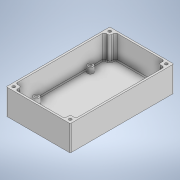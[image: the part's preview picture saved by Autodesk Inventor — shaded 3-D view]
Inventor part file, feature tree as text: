
AUTODESK INVENTOR PART (.ipt)
format: ipt  version: 2021 (Build 250183000, 183)  size: 371,200 bytes
history: native  units: mm
features: fillet x7, extrude x6, sketch x6
ambient origin geometry x8: Origin, YZ Plane, XZ Plane, XY Plane, X Axis, Y Axis, Z Axis, Center Point
bodies: Solid1 (feature_tree)
feature tree (19):
  extrude  "Extrusion1"  Depth=62.0mm
  extrude  "Extrusion2"  Depth=3.0mm
  extrude  "Extrusion3"  Depth=3.0mm
  extrude  "Extrusion4"  Depth=3.0mm
  fillet  "Fillet1"  Radius=6.0mm
  fillet  "Fillet2"  Radius=3.0mm
  fillet  "Fillet3"  Radius=57.4mm
  extrude  "Extrusion5"  Depth=0.8mm
  fillet  "Fillet4"  Radius=51.56mm
  extrude  "Extrusion6"  Depth=6.0mm
  fillet  "Fillet5"  Radius=6.0mm
  fillet  "Fillet6"  Radius=6.0mm
  fillet  "Fillet7"  Radius=20.0mm
  sketch  "Sketch2"  dims[d14=66.0mm d15=62.0mm]
  sketch  "Sketch4"  dims[d16=3.0mm d17=3.0mm]
  sketch  "Sketch5"  dims[d18=3.0mm d19=3.0mm]
  sketch  "Sketch6"  dims[d20=3.0mm d21=4.5mm d22=6.0mm d23=3.0mm d24=57.4mm]
  sketch  "Sketch8"  dims[d25=54.35mm d26=0.8mm d27=51.56mm]
  sketch  "Sketch9"  dims[d28=4.8mm d29=6.0mm d30=6.0mm d31=6.0mm d32=20.0mm d33=20.0mm d34=1.0mm d35=1.0mm d36=2.0mm d37=0.0mm d38=66.0mm d39=62.0mm d40=3.0mm d41=3.0mm d42=3.0mm d43=3.0mm d44=3.0mm d45=4.5mm d46=6.0mm d47=3.0mm d48=57.4mm d49=54.35mm d50=0.8mm d51=51.56mm d52=4.8mm d53=6.0mm d54=6.0mm d55=6.0mm d56=20.0mm d57=20.0mm d58=1.0mm d59=1.0mm d60=0.0mm d61=0.0mm d62=6.0mm d63=0.0mm d64=2.0mm d65=0.0mm d66=2.0mm d67=2.0mm d68=30.0mm d69=4.0mm d70=4.0mm d71=4.0mm d72=2.0mm d73=2.0mm d74=2.0mm d75=2.0mm d76=35.0mm d77=8.0mm d78=0.0mm d79=4.0mm d80=0.0mm d81=1.0mm d82=1.0mm d83=1.0mm d86=2.0mm d87=2.0mm d88=2.0mm d89=2.0mm d90=25.0mm d91=2.0mm d92=0.0mm d93=0.0mm d94=1.0mm d95=3.0mm d96=3.0mm d97=3.0mm d98=3.0mm d99=7.0mm d100=7.0mm d101=7.0mm d102=7.0mm d103=4.0mm d104=4.0mm d105=4.0mm d106=4.0mm d107=4.0mm d108=4.0mm d109=4.0mm d110=4.0mm d111=6.0mm d112=6.0mm d113=6.0mm d114=6.0mm d115=6.0mm d116=6.0mm d117=25.0mm d118=0.0mm d119=2.0mm d120=2.0mm d121=1.0mm]
